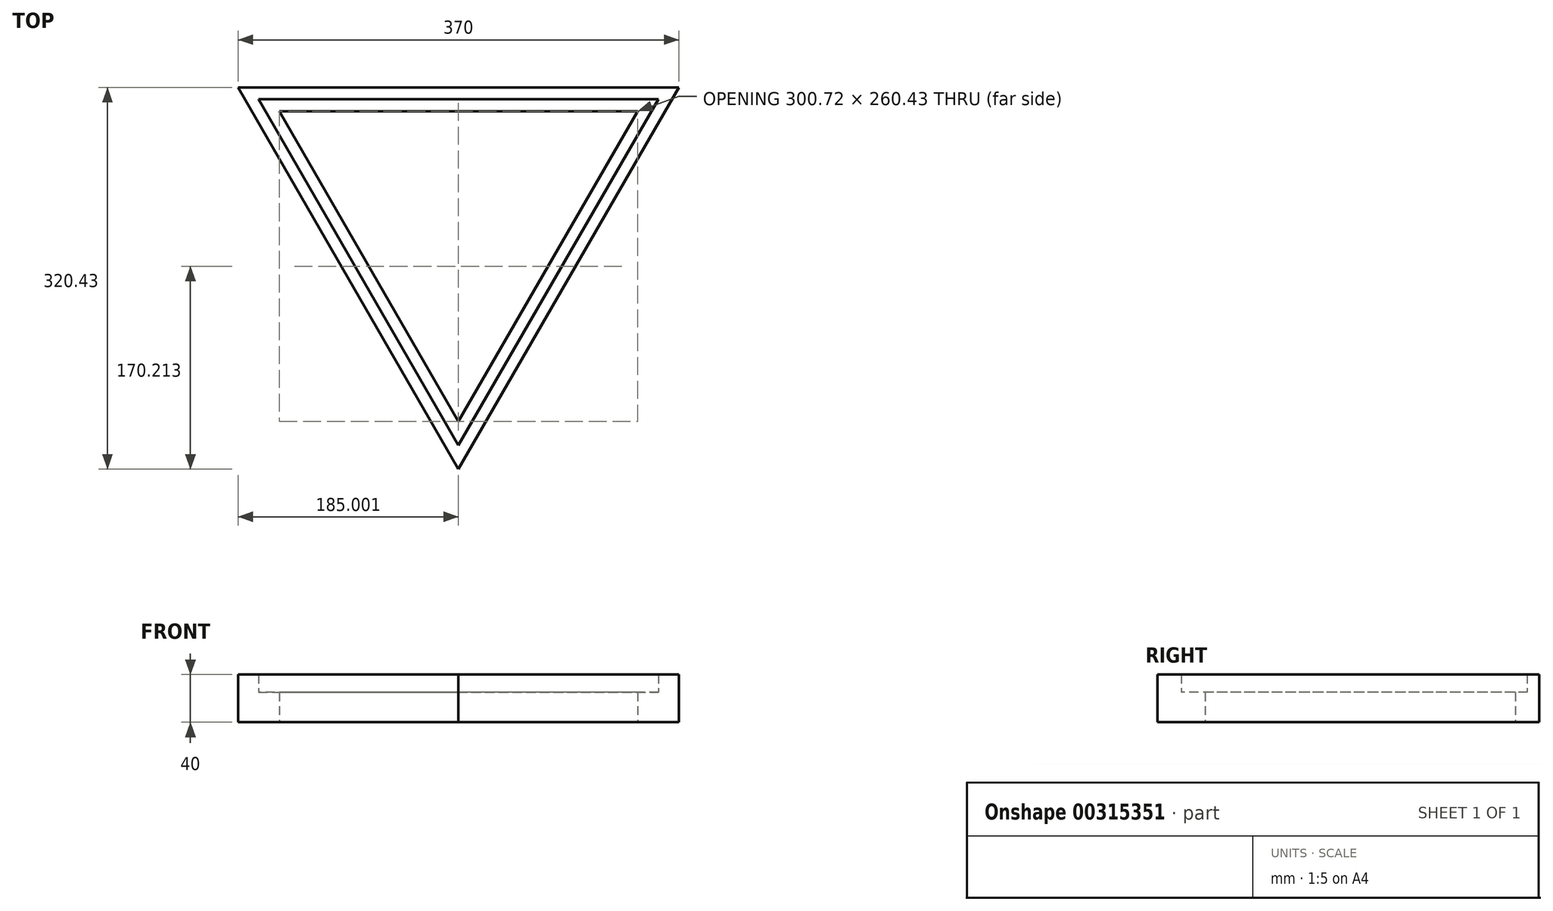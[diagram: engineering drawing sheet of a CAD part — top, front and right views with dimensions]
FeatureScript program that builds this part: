
annotation { "Feature Type Name" : "Feature", "Feature Type Description" : "" }
export const myFeature = defineFeature(function(context is Context, id is Id, definition is map)
    precondition{}
    {
        {
            var Q0;
            Q0=qCreatedBy(makeId("Top.planeOp"),FACE);
            var sketch = newSketch(context, id + "F0", { "sketchPlane" : qUnion([Q0])});
            skLineSegment(sketch, "E0.0", {"start": v(-182.83, 100.95) * mm, "end": v(187.17, 100.95) * mm});
            skLineSegment(sketch, "E0.1", {"start": v(187.17, 100.95) * mm, "end": v(2.17, -219.48) * mm});
            skLineSegment(sketch, "E0.2", {"start": v(2.17, -219.48) * mm, "end": v(-182.83, 100.95) * mm});
            skLineSegment(sketch, "E1.0", {"start": v(2.17, -179.48) * mm, "end": v(-148.19, 80.95) * mm});
            skLineSegment(sketch, "E1.1", {"start": v(152.53, 80.95) * mm, "end": v(2.17, -179.48) * mm});
            skLineSegment(sketch, "E1.2", {"start": v(-148.19, 80.95) * mm, "end": v(152.53, 80.95) * mm});
            skLineSegment(sketch, "E2.0", {"start": v(-165.5, 90.95) * mm, "end": v(169.85, 90.95) * mm});
            skLineSegment(sketch, "E2.1", {"start": v(2.17, -199.48) * mm, "end": v(-165.5, 90.95) * mm});
            skLineSegment(sketch, "E2.2", {"start": v(169.85, 90.95) * mm, "end": v(2.17, -199.48) * mm});
            skSolve(sketch);
        }
        {
            var Q0;
            Q0=makeQuery(id+"F0.imprint","IMPRINT",FACE,{"disambiguationData":[TD([[makeQuery(id+"F0.imprint","IMPRINT",EDGE,{"derivedFrom":sQuery(id+"F0.wireOp",EDGE,"E1.0")}),1.0]])]});
            var Q1;
            Q1=makeQuery(id+"F0.imprint","IMPRINT",FACE,{"disambiguationData":[TD([[makeQuery(id+"F0.imprint","IMPRINT",EDGE,{"derivedFrom":sQuery(id+"F0.wireOp",EDGE,"E0.0")}),-1.0]])]});
            extrude(context, id + "F1", {"entities" : qUnion([Q0, Q1]), "depth" : 25 * mm, "offsetDistance" : 25 * mm});
        }
        {
            var Q0;
            Q0 = qSketchRegion(id + "F0", true);
            extrude(context, id + "F2", {"entities" : qUnion([Q0]), "operationType" : NewBodyOperationType.ADD, "depth" : 40 * mm, "offsetDistance" : 25 * mm});
        }
    });
